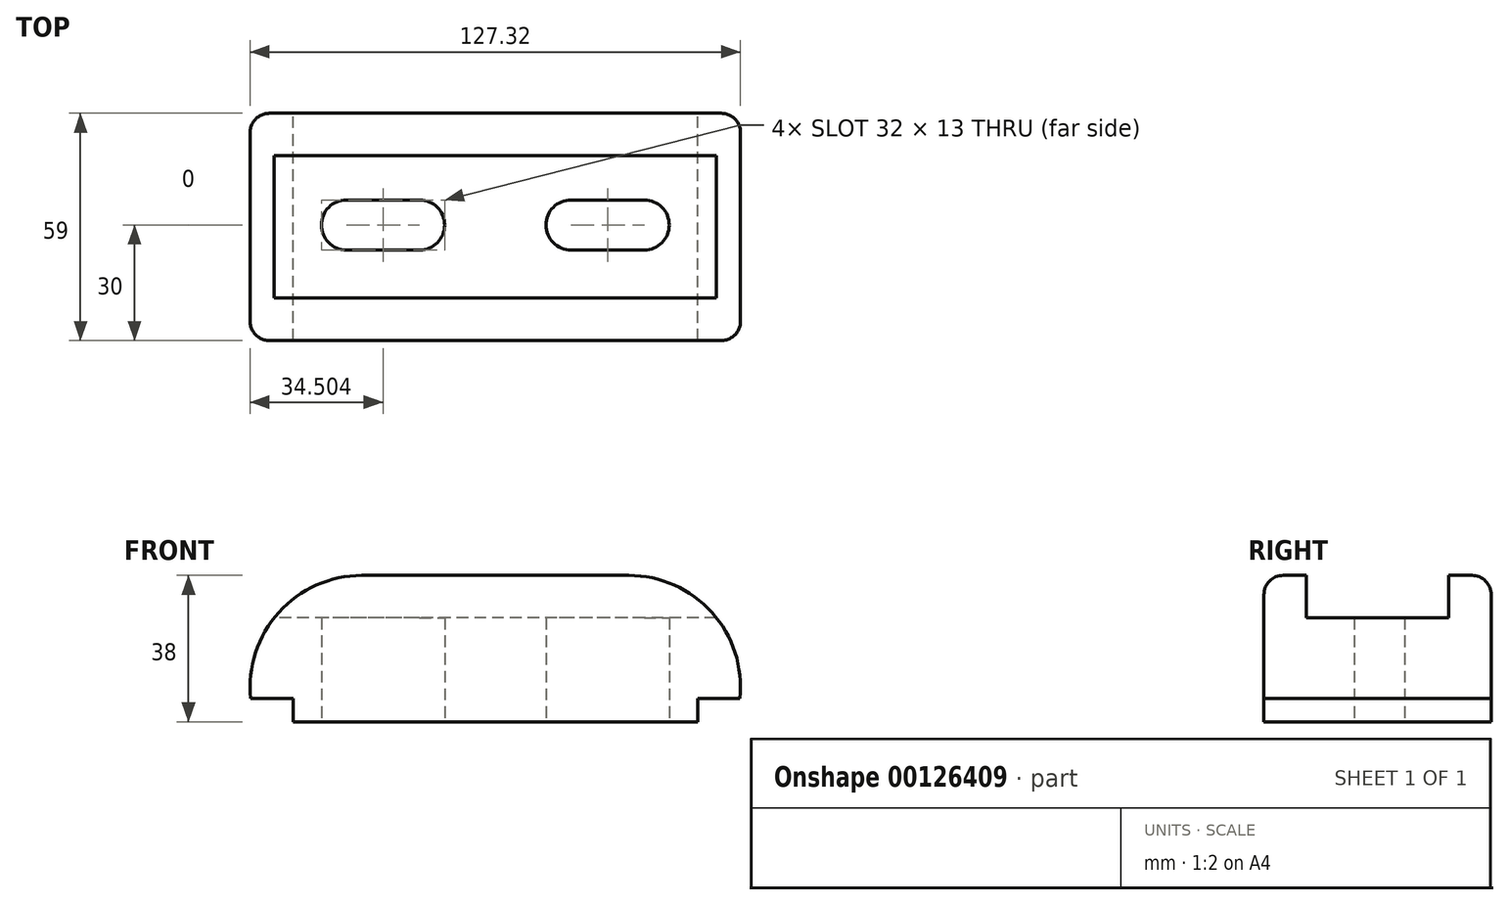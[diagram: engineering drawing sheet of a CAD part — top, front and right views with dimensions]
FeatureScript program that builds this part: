
annotation { "Feature Type Name" : "Feature", "Feature Type Description" : "" }
export const myFeature = defineFeature(function(context is Context, id is Id, definition is map)
    precondition{}
    {
        {
            var Q0;
            Q0=qCreatedBy(makeId("Front.planeOp"),FACE);
            var sketch = newSketch(context, id + "F0", { "sketchPlane" : qUnion([Q0])});
            skLineSegment(sketch, "E0", {"start": v(11, 0) * mm, "end": v(11, 6) * mm});
            skLineSegment(sketch, "E1", {"start": v(11, 6) * mm, "end": v(0, 6) * mm});
            skLineSegment(sketch, "E2", {"start": v(11, 0) * mm, "end": v(116, 0) * mm});
            skLineSegment(sketch, "E3", {"start": v(116, 0) * mm, "end": v(116, 6) * mm});
            skLineSegment(sketch, "E4", {"start": v(116, 6) * mm, "end": v(127, 6) * mm});
            skLineSegment(sketch, "E5", {"start": v(28.84, 38) * mm, "end": v(98.16, 38) * mm});
            skArc(sketch, "E6", {"start": v(28.84, 38) * mm, "mid": v(7.3, 28.42) * mm, "end": v(0, 6) * mm});
            skArc(sketch, "E7", {"start": v(98.16, 38) * mm, "mid": v(119.7, 28.42) * mm, "end": v(127, 6) * mm});
            skSolve(sketch);
        }
        {
            var Q0;
            Q0 = qSketchRegion(id + "F0", true);
            extrude(context, id + "F1", {"entities" : qUnion([Q0]), "depth" : 59 * mm});
        }
        {
            var Q0;
            Q0=qCreatedBy(makeId("Right.planeOp"),FACE);
            var sketch = newSketch(context, id + "F2", { "sketchPlane" : qUnion([Q0])});
            skLineSegment(sketch, "E8", {"start": v(-48, 38) * mm, "end": v(-48, 27) * mm});
            skLineSegment(sketch, "E9", {"start": v(-48, 27) * mm, "end": v(-11, 27) * mm});
            skLineSegment(sketch, "E10", {"start": v(-11, 27) * mm, "end": v(-11, 38) * mm});
            skLineSegment(sketch, "E11.0", {"start": v(-59, 38) * mm, "end": v(0, 38) * mm});
            skSolve(sketch);
        }
        {
            var Q0;
            Q0 = qSketchRegion(id + "F2", true);
            extrude(context, id + "F3", {"entities" : qUnion([Q0]), "operationType" : NewBodyOperationType.REMOVE, "depth" : 170 * mm});
        }
        {
            var Q0;
            Q0=qCreatedBy(makeId("Top.planeOp"),FACE);
            var sketch = newSketch(context, id + "F4", { "sketchPlane" : qUnion([Q0])});
            skLineSegment(sketch, "E12", {"start": v(24.84, -22.5) * mm, "end": v(43.84, -22.5) * mm});
            skLineSegment(sketch, "E13", {"start": v(24.84, -35.5) * mm, "end": v(43.84, -35.5) * mm});
            skLineSegment(sketch, "E14", {"start": v(83.16, -22.5) * mm, "end": v(102.16, -22.5) * mm});
            skLineSegment(sketch, "E15", {"start": v(102.16, -35.5) * mm, "end": v(83.16, -35.5) * mm});
            skArc(sketch, "E16", {"start": v(24.84, -22.5) * mm, "mid": v(18.34, -29) * mm, "end": v(24.84, -35.5) * mm});
            skArc(sketch, "E17", {"start": v(43.84, -22.5) * mm, "mid": v(50.34, -29) * mm, "end": v(43.84, -35.5) * mm});
            skArc(sketch, "E18", {"start": v(83.16, -22.5) * mm, "mid": v(76.66, -29) * mm, "end": v(83.16, -35.5) * mm});
            skArc(sketch, "E19", {"start": v(102.16, -22.5) * mm, "mid": v(108.66, -29) * mm, "end": v(102.16, -35.5) * mm});
            skLineSegment(sketch, "E20", {"start": v(-0.16, -29) * mm, "end": v(127.16, -29) * mm, "construction": true});
            skLineSegment(sketch, "E21", {"start": v(-0.16, -59) * mm, "end": v(-0.16, 0) * mm});
            skLineSegment(sketch, "E22", {"start": v(127.16, 0) * mm, "end": v(127.16, -59) * mm});
            skLineSegment(sketch, "E23.0", {"start": v(98.16, 0) * mm, "end": v(127.16, 0) * mm});
            skLineSegment(sketch, "E24.0", {"start": v(28.84, -59) * mm, "end": v(-0.16, -59) * mm});
            skLineSegment(sketch, "E25.0", {"start": v(28.84, 0) * mm, "end": v(-0.16, 0) * mm});
            skLineSegment(sketch, "E26.0", {"start": v(98.16, -59) * mm, "end": v(127.16, -59) * mm});
            skSolve(sketch);
        }
        {
            var Q0;
            Q0 = qSketchRegion(id + "F4", true);
            extrude(context, id + "F5", {"entities" : qUnion([Q0]), "operationType" : NewBodyOperationType.REMOVE, "depth" : 61.2 * mm});
        }
        {
            var Q0;
            Q0=makeQuery(id+"F1.opExtrude","CAP_EDGE",EDGE,{"disambiguationData":[OSD([sQuery(id+"F0.wireOp",EDGE,"E6")])],"isStart":false});
            var Q1;
            Q1=makeQuery(id+"F1.opExtrude","CAP_EDGE",EDGE,{"disambiguationData":[OSD([sQuery(id+"F0.wireOp",EDGE,"E6")])],"isStart":true});
            fillet(context, id + "F6", {"entities" : qUnion([Q0, Q1]), "radius" : 5 * mm, "tangentPropagation" : true, "allowEdgeOverflow" : false});
        }
    });
